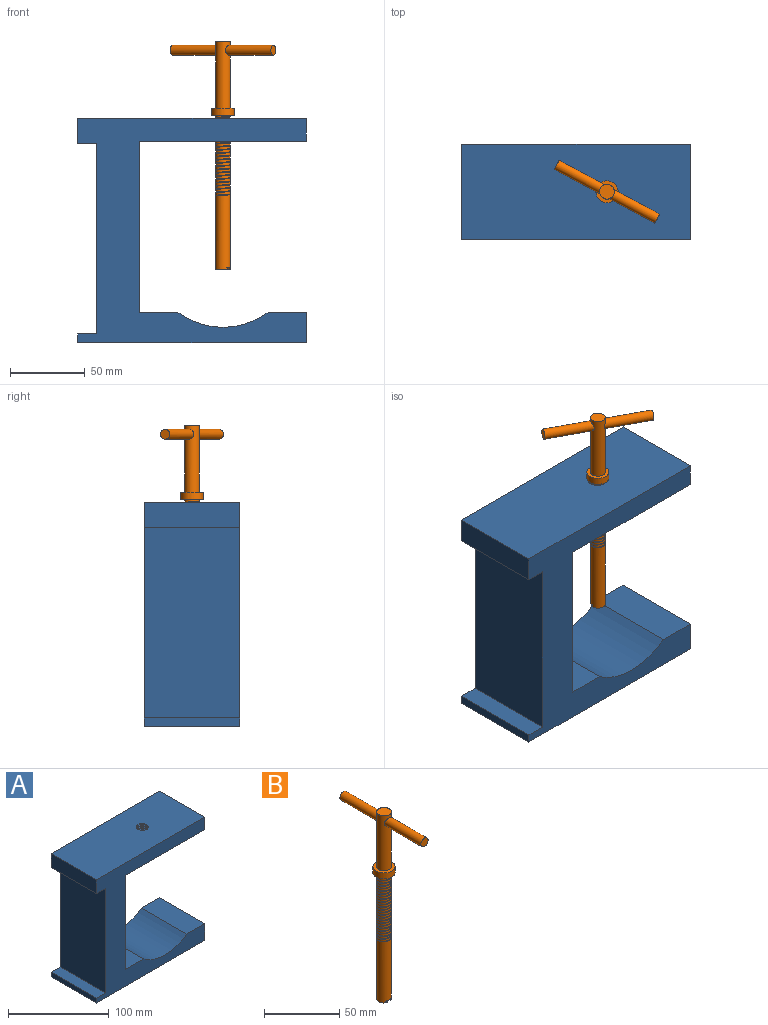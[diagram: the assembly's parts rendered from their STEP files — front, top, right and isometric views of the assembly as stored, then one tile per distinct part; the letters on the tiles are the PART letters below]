
ASSEMBLY  parts=2 mates=1
PART A: 20 faces, bbox 153.7x64.8x152.5 mm
  f0: plane 114.3x63.5mm, normal (1,0,0), area 7258.1mm2, adj f1,f13,f14,f15
  f1: plane 111x63.5mm, normal (0,0,-1), area 6967.3mm2, adj f0,f2,f14,f15,f16
  f2: plane 63.5x15.24mm, normal (1,0,0), area 967.7mm2, adj f1,f3,f14,f15
  f3: plane 153.67x64.77mm, normal (0,0,1), area 9579.4mm2, adj f2,f4,f14,f15,f16,f18,f19
  f4: plane 63.5x16.92mm, normal (-1,0,0), area 1074.2mm2, adj f3,f5,f14,f15
  f5: plane 63.5x12.7mm, normal (0,0,-1), area 806.5mm2, adj f4,f6,f14,f15
  f6: plane 127x63.5mm, normal (-1,0,0), area 8064.5mm2, adj f5,f7,f14,f15
  f7: plane 63.5x12.7mm, normal (0,0,1), area 806.5mm2, adj f6,f8,f14,f15
  f8: plane 63.5x5.82mm, normal (-1,0,0), area 369.6mm2, adj f7,f9,f14,f15
  f9: plane 152.4x63.5mm, normal (0,0,-1), area 9677.4mm2, adj f8,f10,f14,f15
  f10: plane 63.5x20.2mm, normal (1,0,0), area 1282.4mm2, adj f9,f11,f14,f15
  f11: plane 63.5x25.4mm, normal (0,0,1), area 1612.9mm2, adj f10,f12,f14,f15
  f12: cylinder r=50.8mm len=63.5mm, axis (0,1,0), area 4091.4mm2, adj f11,f13,f14,f15
  f13: plane 63.5x25.4mm, normal (0,0,1), area 1612.9mm2, adj f0,f12,f14,f15
  f14: plane 152.4x149.74mm, normal (0,-1,0), area 8114.9mm2, adj f0,f1,f2,f3,f4,f5,f6,f7
  f15: plane 152.4x149.74mm, normal (0,1,0), area 8114.9mm2, adj f0,f1,f2,f3,f4,f5,f6,f7
  f16: cylinder r=5.08mm len=15.24mm, axis (0,0,1), area 161.8mm2, adj f1,f3,f17,f18,f19
  f17: plane 1.8x1.37mm, normal (0,1,0), area 1.2mm2, adj f16,f18,f19
  f18: bspline ~16.74x14.9mm, area 419.6mm2, adj f3,f16,f17,f19
  f19: bspline ~14.9x14.41mm, area 272.6mm2, adj f3,f16,f17,f18
PART B: 47 faces, bbox 15.2x76.6x153 mm
  f0: cylinder r=4.95mm len=9.91mm, axis (0,0,1), area 52.3mm2, adj f1,f25,f36,f37
  f1: cylinder r=4.95mm len=9.91mm, axis (0,0,1), area 52.3mm2, adj f0,f2,f36,f37
  f2: cylinder r=4.95mm len=9.91mm, axis (0,0,1), area 52.3mm2, adj f1,f3,f36,f37
  f3: cylinder r=4.95mm len=9.91mm, axis (0,0,1), area 52.3mm2, adj f2,f4,f36,f37
  f4: cylinder r=4.95mm len=9.91mm, axis (0,0,1), area 52.3mm2, adj f3,f5,f36,f37
  f5: cylinder r=4.95mm len=9.91mm, axis (0,0,1), area 52.3mm2, adj f4,f6,f36,f37
  f6: cylinder r=4.95mm len=9.91mm, axis (0,0,1), area 52.3mm2, adj f5,f7,f36,f37
  f7: cylinder r=4.95mm len=9.91mm, axis (0,0,1), area 52.3mm2, adj f6,f8,f36,f37
  f8: cylinder r=4.95mm len=9.91mm, axis (0,0,1), area 52.3mm2, adj f7,f9,f36,f37
  f9: cylinder r=4.95mm len=9.91mm, axis (0,0,1), area 52.3mm2, adj f8,f10,f36,f37
  f10: cylinder r=4.95mm len=9.91mm, axis (0,0,1), area 52.3mm2, adj f9,f11,f36,f37
  f11: cylinder r=4.95mm len=9.91mm, axis (0,0,1), area 52.3mm2, adj f10,f12,f36,f37
  f12: cylinder r=4.95mm len=9.91mm, axis (0,0,1), area 52.3mm2, adj f11,f13,f36,f37
  f13: cylinder r=4.95mm len=9.91mm, axis (0,0,1), area 52.3mm2, adj f12,f14,f36,f37
  f14: cylinder r=4.95mm len=9.91mm, axis (0,0,1), area 52.3mm2, adj f13,f15,f36,f37
  f15: cylinder r=4.95mm len=9.91mm, axis (0,0,1), area 52.3mm2, adj f14,f16,f36,f37
  f16: cylinder r=4.95mm len=9.91mm, axis (0,0,1), area 52.3mm2, adj f15,f17,f36,f37
  f17: cylinder r=4.95mm len=9.91mm, axis (0,0,1), area 52.3mm2, adj f16,f18,f36,f37
  f18: cylinder r=4.95mm len=9.91mm, axis (0,0,1), area 52.3mm2, adj f17,f19,f36,f37
  f19: cylinder r=4.95mm len=9.91mm, axis (0,0,1), area 52.3mm2, adj f18,f20,f36,f37
  f20: cylinder r=4.95mm len=9.91mm, axis (0,0,1), area 52.3mm2, adj f19,f21,f36,f37
  f21: cylinder r=4.95mm len=9.91mm, axis (0,0,1), area 52.3mm2, adj f20,f22,f36,f37
  f22: cylinder r=4.95mm len=9.91mm, axis (0,0,1), area 52.3mm2, adj f21,f23,f36,f37
  f23: cylinder r=4.95mm len=9.91mm, axis (0,0,1), area 52.3mm2, adj f22,f24,f36,f37
  f24: cylinder r=4.95mm len=9.91mm, axis (0,0,1), area 33.7mm2, adj f23,f34,f36,f39
  f25: cylinder r=4.95mm len=50.65mm, axis (0,0,1), area 1528.6mm2, adj f0,f26,f28,f29,f30,f31,f32,f33
  f26: cone r=3.85mm half-angle=36.8deg, axis (0,0,-1), area 31.7mm2, adj f25,f27,f28,f29,f30,f31,f32,f33
  f27: plane 7.71x7.71mm, normal (0,0,-1), area 46.7mm2, adj f26
  f28: plane 5.97x3.15mm, normal (0,0,-1), area 7.2mm2, adj f25,f26,f29,f30
  f29: plane 3.16x1.87mm, normal (-0.71,0,0.71), area 1.5mm2, adj f25,f26,f28
  f30: plane 2.17x1.7mm, normal (0.71,0,0.71), area 1.3mm2, adj f25,f26,f28
  f31: plane 2.17x1.7mm, normal (0.71,0,0.71), area 1.3mm2, adj f25,f26,f32
  f32: plane 5.97x3.15mm, normal (0,0,-1), area 7.2mm2, adj f25,f26,f31,f33
  f33: plane 3.16x1.87mm, normal (-0.71,0,0.71), area 1.5mm2, adj f25,f26,f32
  f34: plane 0.48x0.35mm, normal (0,-1,0), area 0.1mm2, adj f24,f36,f37
  f35: plane 0.48x0.35mm, normal (0,1,0), area 0.1mm2, adj f25,f36,f37
  f36: bspline ~54.53x11.44mm, area 413.2mm2, adj f0,f1,f2,f3,f4,f5,f6,f7
  f37: bspline ~54.19x11.89mm, area 266mm2, adj f0,f1,f2,f3,f4,f5,f6,f7
  f38: cylinder r=7.39mm len=14.79mm, axis (0,0,-1), area 224.2mm2, adj f39,f40
  f39: plane 14.79x14.79mm, normal (0,0,-1), area 94.7mm2, adj f24,f38
  f40: plane 14.79x14.79mm, normal (0,0,1), area 94.7mm2, adj f38,f43
  f41: cylinder r=3.39mm len=33.15mm, axis (0,1,0), area 706.9mm2, adj f42,f43
  f42: plane 6.79x6.79mm, normal (0,-1,0), area 36.2mm2, adj f41
  f43: cylinder r=4.95mm len=44.7mm, axis (0,0,-1), area 1313.6mm2, adj f40,f41,f44,f46
  f44: plane 9.91x9.91mm, normal (0,0,1), area 77.1mm2, adj f43
  f45: plane 6.79x6.79mm, normal (0,1,0), area 36.2mm2, adj f46
  f46: cylinder r=3.39mm len=33.15mm, axis (0,1,0), area 706.9mm2, adj f43,f45
PLACE A t=(-350.98,157.57,8.67)mm fixed
PLACE B rot(axis=(0,0,1),61.9deg) t=(-313.45,188.15,-7.29)mm
MATE cylindrical A.f16 <-> B.f26  axis (0,0,1) through (-329.77,157.57,81.25)mm
